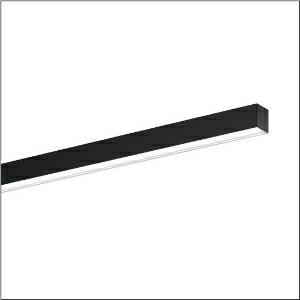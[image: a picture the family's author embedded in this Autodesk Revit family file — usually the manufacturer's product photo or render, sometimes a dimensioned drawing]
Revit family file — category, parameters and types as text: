
# Revit family: silica_r__21_51mx23db45bb_2d31
name_source: partatom
category: Lighting Fixtures
units: mm (PartAtom-declared; Revit-internal decimal feet)

## family parameters
Cut with Voids When Loaded = No
Host = Face
Light Source = No
Part Type = Normal
Room Calculation Point = No
Round Connector Dimension = Use Diameter
Shared = No

## types (1)
- --- (1 x LED, 4100 lm, 28.1 W, 4000K)
    Apparent Load = 28 VA
    CIE Flux Codes = 78 96 99 100 100
    Color Rendering = 80
    Color Temperature = 4000K
    Default Elevation = 1800 mm
    Description = Silica® 21, office luminaire, primary optical cover: prismatic diffuser, of PMMA, CAT 2 (L<= 3000cd/m²), light emission: direct distribution, primary light characteristic: symmetric, installation type: surface-mounted, LED, rated luminous flux: 4.100lm, luminous efficacy: 146lm/W, light colour: 840, colour temperature: 4000K, control gear: DALI 2, with terminal, 3+2-pole, max. 2.5mm², mains connection: 220..240V, AC, 50/60Hz, rated input power: 28.1W, luminaire housing, of aluminium, matt jet black (RAL 9005), length: 1.504mm, width: 53mm, height: 53mm, protection rating (complete): IP20, insulation class (complete): insulation class I (protective earthing), certification: CE, permissible operating ambient temperature: 0..+35°C, standard: EN 50419, packaging unit: 1 piece
    Height = 53 mm
    Lamp = 1 x LED
    Lamp Light Flux = 4100 lm
    Lamp Power = 28.1 W
    Lamp count = 1
    Length = 1504 mm
    Luminous efficacy = 146 lm/W
    Manufacturer = Siteco
    ModVariant = No
    Model = 51MX23DB45BB
    Mounting Place = Ceiling
    Mounting Type = Surface mounted
    Number of Poles = 1
    OnlyDefault = Yes
    Power Factor = 1
    Product Name = Silica® 21
    Product group = office luminaire | ceiling mounted
    ProductGroupID = 303
    Protection Class = Protection class I
    Protection Degree = IP 20
    RLX_Detail_Level = 1
    RLX_Emergency_Light_Flux = 0 lm
    RLX_Emergency_Type = 0
    RLX_Emergency_Type_DB = No
    RlxData = <blob elided: 23785 chars, md5=f58ee78a>
    Socket = socket
    Standby Power = 0 W
    System Light Flux = 4100 lm
    System Power = 28 W
    Type Comments = factory setting: luminous flux: 100 % | dim-lin: 254 | 323 mA
    Type Image = l_1335925.jpg
    URL = http://relux.com
    VarID = @adj_140943
    Voltage = 0 V
    Weight = 0.00 kg
    Width = 53 mm

## geometry (parser evidence)
native form markers: Blend x4, Sweep x11
no freeform markers — native parametric forms only
